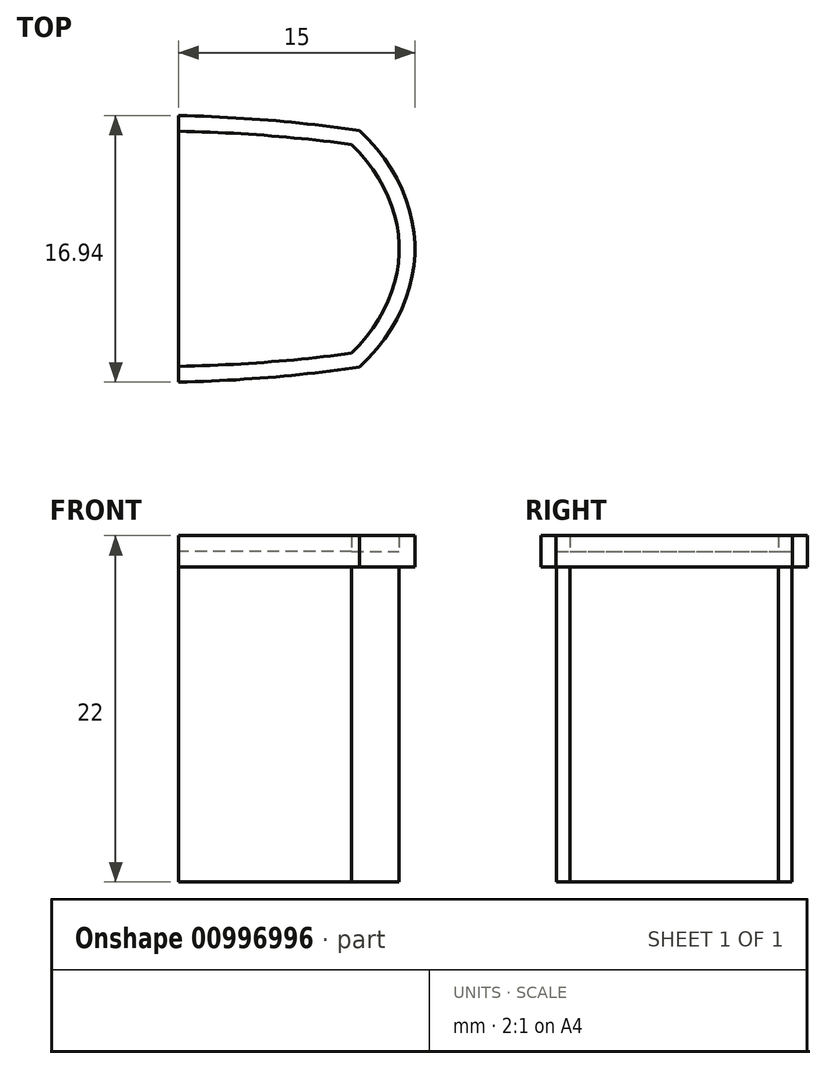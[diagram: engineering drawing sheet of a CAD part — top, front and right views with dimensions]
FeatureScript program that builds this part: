
annotation { "Feature Type Name" : "Feature", "Feature Type Description" : "" }
export const myFeature = defineFeature(function(context is Context, id is Id, definition is map)
    precondition{}
    {
        {
            var Q0;
            Q0=qCreatedBy(makeId("Top.planeOp"),FACE);
            var sketch = newSketch(context, id + "F0", { "sketchPlane" : qUnion([Q0])});
            skEllipse(sketch, "E0", {"center": v(0, 0) * mm, "majorRadius": 17.5 * mm, "minorRadius": 12.5 * mm, "majorAxis": v(-1, 0)});
            skEllipse(sketch, "E1", {"center": v(0, 0) * mm, "majorRadius": 29.75 * mm, "minorRadius": 8.5 * mm, "majorAxis": v(-1, 0)});
            skPoint(sketch, "E2", {"position": v(14, -7.5) * mm});
            skPoint(sketch, "E3", {"position": v(14, 7.5) * mm});
            skPoint(sketch, "E4", {"position": v(-14, 7.5) * mm});
            skPoint(sketch, "E5", {"position": v(-14, -7.5) * mm});
            skLineSegment(sketch, "E6", {"start": v(2.5, -8.47) * mm, "end": v(2.5, 8.47) * mm});
            skLineSegment(sketch, "E7", {"start": v(2.5, 0) * mm, "end": v(17.5, 0) * mm});
            skPoint(sketch, "E8", {"position": v(-17.5, 0) * mm});
            skEllipse(sketch, "E9", {"center": v(0, 0) * mm, "majorRadius": 28.75 * mm, "minorRadius": 7.5 * mm, "majorAxis": v(-1, 0)});
            skEllipse(sketch, "E10", {"center": v(0, 0) * mm, "majorRadius": 16.5 * mm, "minorRadius": 11.5 * mm, "majorAxis": v(1, 0)});
            skSolve(sketch);
        }
        {
            var Q0;
            {var subQ0=sQuery(id+"F0.wireOp",EDGE,"E7");var subQ1=sQuery(id+"F0.wireOp",EDGE,"E6");var subQ2=makeQuery(id+"F0.imprint","INTERSECT",VERTEX,{"derivedFrom":[subQ1,subQ0]});Q0=makeQuery(id+"F0.imprint","IMPRINT",FACE,{"disambiguationData":[TD([[makeQuery(id+"F0.imprint","IMPRINT",EDGE,{"disambiguationData":[TD([[subQ2,1.0]])],"derivedFrom":subQ1}),-1.0]])]});}
            var Q1;
            {var subQ0=sQuery(id+"F0.wireOp",EDGE,"E7");var subQ1=sQuery(id+"F0.wireOp",EDGE,"E6");var subQ2=makeQuery(id+"F0.imprint","INTERSECT",VERTEX,{"derivedFrom":[subQ1,subQ0]});Q1=makeQuery(id+"F0.imprint","IMPRINT",FACE,{"disambiguationData":[TD([[makeQuery(id+"F0.imprint","IMPRINT",EDGE,{"disambiguationData":[TD([[subQ2,-1.0]])],"derivedFrom":subQ1}),-1.0]])]});}
            extrude(context, id + "F1", {"entities" : qUnion([Q0, Q1]), "depth" : 26 * mm, "offsetDistance" : 25 * mm, "hasSecondDirection" : true, "secondDirectionOppositeDirection" : false, "secondDirectionDepth" : 5 * mm});
        }
        {
            var Q0;
            {var subQ0=sQuery(id+"F0.wireOp",EDGE,"E6");var subQ1=sQuery(id+"F0.wireOp",EDGE,"E1");var subQ2=makeQuery(id+"F0.imprint","INTERSECT",VERTEX,{"disambiguationData":[OD(0.0)],"derivedFrom":[subQ1,subQ0]});Q0=makeQuery(id+"F0.imprint","IMPRINT",FACE,{"disambiguationData":[TD([[makeQuery(id+"F0.imprint","IMPRINT",EDGE,{"disambiguationData":[TD([[subQ2,-1.0]])],"derivedFrom":subQ1}),1.0]])]});}
            var Q1;
            {var subQ0=sQuery(id+"F0.wireOp",EDGE,"E6");var subQ1=sQuery(id+"F0.wireOp",EDGE,"E1");var subQ2=makeQuery(id+"F0.imprint","INTERSECT",VERTEX,{"disambiguationData":[OD(1.0)],"derivedFrom":[subQ1,subQ0]});Q1=makeQuery(id+"F0.imprint","IMPRINT",FACE,{"disambiguationData":[TD([[makeQuery(id+"F0.imprint","IMPRINT",EDGE,{"disambiguationData":[TD([[subQ2,1.0]])],"derivedFrom":subQ1}),1.0]])]});}
            var Q2;
            {var subQ0=sQuery(id+"F0.wireOp",EDGE,"E7");var subQ1=sQuery(id+"F0.wireOp",EDGE,"E0");var subQ2=makeQuery(id+"F0.imprint","INTERSECT",VERTEX,{"derivedFrom":[subQ1,subQ0]});Q2=makeQuery(id+"F0.imprint","IMPRINT",FACE,{"disambiguationData":[TD([[makeQuery(id+"F0.imprint","IMPRINT",EDGE,{"disambiguationData":[TD([[subQ2,1.0]])],"derivedFrom":subQ1}),1.0]])]});}
            var Q3;
            {var subQ0=sQuery(id+"F0.wireOp",EDGE,"E7");var subQ1=sQuery(id+"F0.wireOp",EDGE,"E0");var subQ2=makeQuery(id+"F0.imprint","INTERSECT",VERTEX,{"derivedFrom":[subQ1,subQ0]});Q3=makeQuery(id+"F0.imprint","IMPRINT",FACE,{"disambiguationData":[TD([[makeQuery(id+"F0.imprint","IMPRINT",EDGE,{"disambiguationData":[TD([[subQ2,-1.0]])],"derivedFrom":subQ1}),1.0]])]});}
            var Q4;
            {var subQ0=sQuery(id+"F0.wireOp",EDGE,"E1");var subQ1=sQuery(id+"F0.wireOp",EDGE,"E0");var subQ2=makeQuery(id+"F0.imprint","INTERSECT",VERTEX,{"disambiguationData":[OD(1.0)],"derivedFrom":[subQ1,subQ0]});Q4=makeQuery(id+"F0.imprint","IMPRINT",FACE,{"disambiguationData":[TD([[makeQuery(id+"F0.imprint","IMPRINT",EDGE,{"disambiguationData":[TD([[subQ2,-1.0]])],"derivedFrom":subQ1}),1.0]])]});}
            var Q5;
            {var subQ0=sQuery(id+"F0.wireOp",EDGE,"E1");var subQ1=sQuery(id+"F0.wireOp",EDGE,"E0");var subQ2=makeQuery(id+"F0.imprint","INTERSECT",VERTEX,{"disambiguationData":[OD(2.0)],"derivedFrom":[subQ1,subQ0]});Q5=makeQuery(id+"F0.imprint","IMPRINT",FACE,{"disambiguationData":[TD([[makeQuery(id+"F0.imprint","IMPRINT",EDGE,{"disambiguationData":[TD([[subQ2,1.0]])],"derivedFrom":subQ1}),1.0]])]});}
            extrude(context, id + "F2", {"entities" : qUnion([Q0, Q1, Q2, Q3, Q4, Q5]), "operationType" : NewBodyOperationType.ADD, "depth" : 27 * mm, "offsetDistance" : 25 * mm, "hasSecondDirection" : true, "secondDirectionOppositeDirection" : false, "secondDirectionDepth" : 25 * mm});
        }
        {
            var Q0;
            {var subQ0=sQuery(id+"F0.wireOp",EDGE,"E7");var subQ1=sQuery(id+"F0.wireOp",EDGE,"E6");var subQ2=makeQuery(id+"F0.imprint","INTERSECT",VERTEX,{"derivedFrom":[subQ1,subQ0]});Q0=makeQuery(id+"F0.imprint","IMPRINT",FACE,{"disambiguationData":[TD([[makeQuery(id+"F0.imprint","IMPRINT",EDGE,{"disambiguationData":[TD([[subQ2,-1.0]])],"derivedFrom":subQ1}),-1.0]])]});}
            var Q1;
            {var subQ0=sQuery(id+"F0.wireOp",EDGE,"E7");var subQ1=sQuery(id+"F0.wireOp",EDGE,"E6");var subQ2=makeQuery(id+"F0.imprint","INTERSECT",VERTEX,{"derivedFrom":[subQ1,subQ0]});Q1=makeQuery(id+"F0.imprint","IMPRINT",FACE,{"disambiguationData":[TD([[makeQuery(id+"F0.imprint","IMPRINT",EDGE,{"disambiguationData":[TD([[subQ2,1.0]])],"derivedFrom":subQ1}),-1.0]])]});}
            extrude(context, id + "F3", {"entities" : qUnion([Q0, Q1]), "depth" : 27 * mm, "offsetDistance" : 25 * mm, "hasSecondDirection" : true, "secondDirectionOppositeDirection" : false, "secondDirectionDepth" : 26 * mm});
        }
    });
